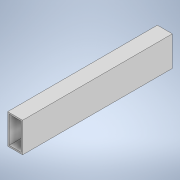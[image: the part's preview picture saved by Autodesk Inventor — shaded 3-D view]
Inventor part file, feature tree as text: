
AUTODESK INVENTOR PART (.ipt)
format: ipt  version: 2020 (Build 240168000, 168)  size: 96,256 bytes
history: native  units: in
note: dims shown in document units (in); Inventor stores cm internally (conversion verified against a paired STEP export)
features: extrude x1, sketch x1
ambient origin geometry x8: Origin, YZ Plane, XZ Plane, XY Plane, X Axis, Y Axis, Z Axis, Center Point
bodies: Solid1 (feature_tree)
feature tree (2):
  extrude  "Extrusion1"  Depth=2.0in
  sketch  "Sketch1"  dims[d0=1.0in d1=2.0in d2=0.1in d3=10.0in d4=0.0in]
